# Revit family: IS_BlendCube_T3686_BIM_NL
name_source: partatom
category: Plumbing Fixtures
units: mm (PartAtom-declared; Revit-internal decimal feet)

## family parameters
Always vertical = No
Cut with Voids When Loaded = No
OmniClass Number = 23.45.05.21.11.11
OmniClass Title = Water Operated Water Closets
Part Type = Normal
Room Calculation Point = No
Round Connector Dimension = Use Diameter
Shared = No
Work Plane-Based = No

## types (1)
- T368601 - Blend Cube Wall Hung Bowl, Aquablade, Hidden Fixation, Glossy White
    Accesoires = https://www.idealstandard.nl
    Accessories = https://www.idealstandard.nl
    Afmetingen = 355 x 540 x 344 mm
    Afwerking = Wit
    AreaUnits = millimetres
    Artikelnummer = T368601
    Artikelomschrijving = Wandtiefspül-WC Blend Cube AquaBlade 355x540x350mm Weiß
    Artikelreferentie = Wandtiefspül-WC Blend Cube AquaBlade 355x540x350mm Weiß
    Auteur = Ideal Standard
    BIMObjectName = IS_IdealStandard_WC pans_BlendCube_T3686
    BIMobject category = Toilets
    BIMobject category code = sanitary-toilets
    BIMobject main category = Sanitary
    BIMobject main category code = sanitary
    BarCode = 8014140467540
    Barcode = 8014140467540
    Beschrijvinggarantie = Herstellergarantie
    Bestanddelen = Wandtiefspül-WC _DE AquaBlade 355x540x350mm Weiß
    BimObjectNaam = IS_IdealStandard_WC pans_BlendCube_T3686
    Brand = Ideal Standard
    Brand url = https://www.idealstandard.nl
    Breedte = 0
    BrutoGewicht = 0
    Color = White
    ConnectionType = Plumbing
    Cost = 0 $
    CurrencyUnit = €
    CurrentRevision = 1
    Date of publishing = 30/04/2021
    Description = Blend Cube Wall Hung Bowl, Aquablade, Hidden Fixation, Glossy White
    Diepte = 540 mm
    DurationUnit = Years
    DuurEenheid = Jahre
    Edition number = 1
    Eigenschappen = Wandtiefspül-WC Blend Cube AquaBlade 355x540x350mm Weiß
    ExpectedLife = 99
    Features = Wall Hung Bowl with Aquablade flushing technology, with Hidden Fixation in Glossy White finish
    Finish = White
    GTIN code = https://8014140467540
    Garantieunits = Jahre
    GemaaktOp = 26/04/2021
    Help = https://www.idealstandard.nl
    Hoogte = 343.97388
    Hulp = https://www.idealstandard.nl
    IFC Classification = Sanitary Terminal
    IfcExportAs = IfcSanitaryTerminalType
    IfcExportType = TOILETPAN
    Installatieinstructies = https://www.idealstandard.nl
    Installation instructions = https://www.idealstandard.nl
    InstallationInstructions = https://www.idealstandard.nl
    Kleur = Weiß
    Kleurwc = Weiß
    Lengte = 0 mm  [stored 0 ft]
    LinearUnits = millimetres
    MainColor = White
    MaintenanceInformation = https://www.idealstandard.nl
    Manufacturer = Ideal Standard Nederland BV
    Manufacturer name = Ideal Standard
    ManufacturerURL = https://www.idealstandard.nl
    Masterformat 2014 Code = 12 46 16
    Masterformat 2014 Description = Bowls
    Materiaal = Glasachtig porselein
    MateriaalWC = Glasachtig porselein
    Material = Vitreous China
    Material main = Vitreous china
    Merk = Ideal Standard
    Model = T368601
    ModelNumber = T368601
    ModelReference = Blend Cube Wall Hung Bowl, Aquablade, Hidden Fixation, Glossy White
    Montageinstuctie = https://www.idealstandard.nl
    NBS Reference Code = 45-35-70/384
    NBS Reference Description = Wc Pans
    Name = WC pans_BlendCube_T3686_IdealStandard
    NettWeight = 26.6
    Nettogewicht = 26.6
    NominalDepth = 540 mm
    NominalHeight = 344 mm
    NominalWidth = 355 mm
    Normen = WC pans_BlendCube_T3686_IdealStandard
    OmniClass Code = 23-31 19 00
    OmniClass Description = Toilets
    OppervlakteEenheid = Millimeter
    Overloop = 0 mm  [stored 0 ft]
    PanColor = White
    PanMaterial = Vitreous China
    PanMounting = Wall Hung
    PredefinedType = WC Pan
    Product Guid = c47c96d1-0e98-47c5-97f3-b46528a9d0fb
    Product SKU = T3686
    Product certification = https://www.idealstandard.nl
    Product data url = https://bimobject.com
    Product family = Blend Cube
    Product group = WC Bowls
    Product name = Blend Cube wall hung Aquablade WC Bowl
    Product url = https://www.idealstandard.nl
    ProductInformation = https://www.idealstandard.nl
    ProductSoort = Sanitärartikel
    Productinformatie = https://www.idealstandard.nl
    QR code = http://bimobject.com
    Referentie = T368601
    Revisie = 1
    SeatHasCover = No
    Shape = Sculpture
    Size = 355 x 540 x 344 mm
    Space = Internal
    SpareParts = https://www.idealstandard.nl
    Technical description = https://www.idealstandard.nl
    Telefoonnummer = 0049 228 5210
    ToiletPanType = Aquablade
    ToiletType = Wall Hung Bowl, Aquablade, Hidden Fixation
    Typeconnectie = Installation
    UNSPSC Code = 30181511
    URL = https://www.idealstandard.nl
    Uniclass 1.4 Code = L7216
    Uniclass 1.4 Description = Toilets
    Uniclass 2.0 Code = PR-35-93-94
    Uniclass 2.0 Description = Wc Pans
    Uniclass 2015 Code = Pr_40_20_93_94
    Uniclass 2015 Name = WC pans
    Uniclass2015Version = v1.20
    Uniformat II Code = D2010
    Uniformat II Description = Plumbing Fixtures
    Urlproducent = https://www.idealstandard.nl
    ValutaEenheid = €
    Versie = 1
    Version = 1
    Vervangingskosten = 0
    VolumeUnits = Liters
    Volumeunits = Liter
    Vorm = Skulptur
    WRASURL = https://www.wrasapprovals.co.uk
    WarrantyDescription = Manufacturer Warranty
    WarrantyDurationParts = 99
    WarrantyDurationUnit = Years
    Wisselstukken = https://www.idealstandard.nl
    Youtube clip = https://www.youtube.com

note: [stored X ft] marks values corroborated as IEEE doubles in the binary element streams (Revit-internal decimal feet)

## geometry (parser evidence)
native form markers: Blend x29, Sweep x3
no freeform markers — native parametric forms only
